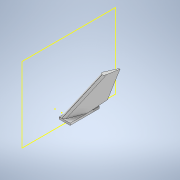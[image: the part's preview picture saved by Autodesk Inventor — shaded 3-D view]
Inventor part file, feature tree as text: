
AUTODESK INVENTOR PART (.ipt)
format: ipt  version: 2020 (Build 240168000, 168)  size: 125,952 bytes
history: native  units: mm
features: other x3, sketch x2
ambient origin geometry x8: Origin, YZ Plane, XZ Plane, XY Plane, X Axis, Y Axis, Z Axis, Center Point
bodies: Solid1 (feature_tree)
feature tree (5):
  other  "Tall KauriSpoilerFin.ipt"
  other  "Solid1::Tall KauriSpoilerFin.ipt"
  other  "TaggingFeature1"
  sketch  "Sketch9"  dims[d0=10.0mm]
  sketch  "Sketch13"
